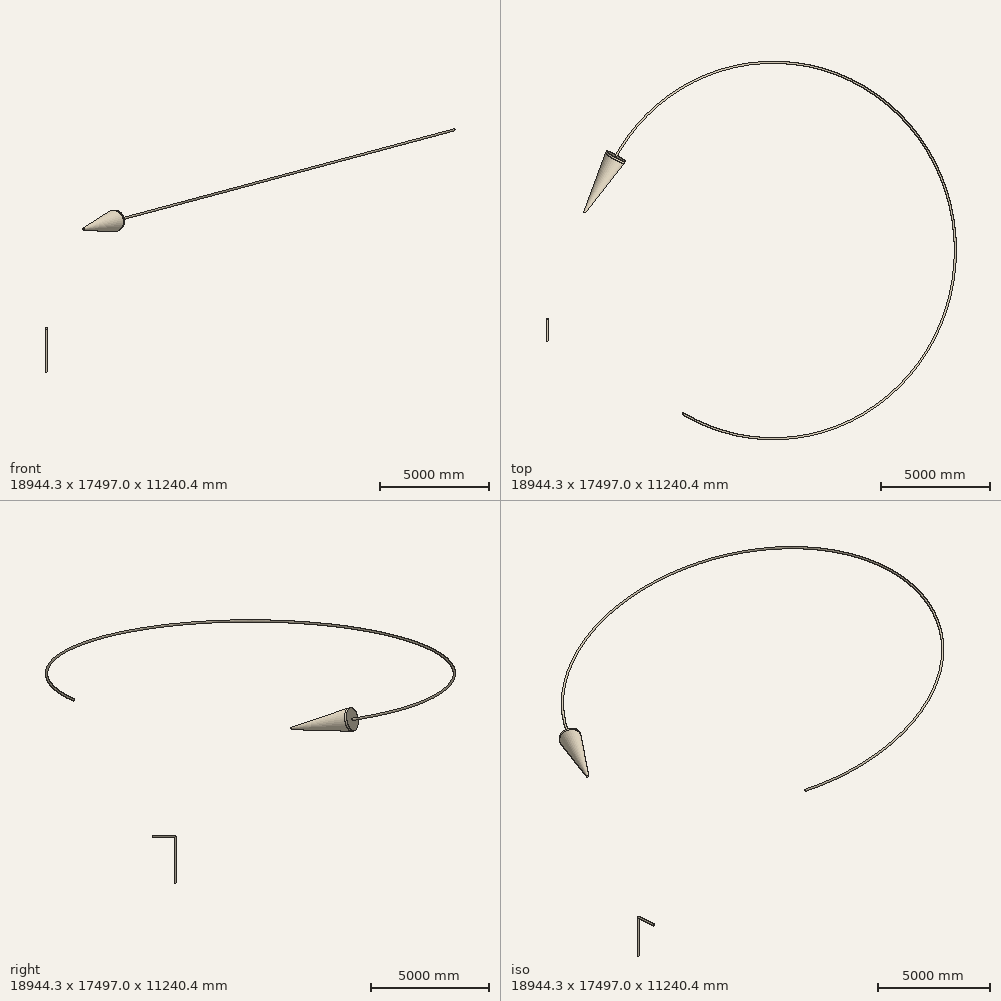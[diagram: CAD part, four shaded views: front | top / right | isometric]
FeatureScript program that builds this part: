
annotation { "Feature Type Name" : "Feature", "Feature Type Description" : "" }
export const myFeature = defineFeature(function(context is Context, id is Id, definition is map)
    precondition{}
    {
        {
            var Q0;
            Q0=qCreatedBy(makeId("Top.planeOp"),FACE);
            var sketch = newSketch(context, id + "F0", { "sketchPlane" : qUnion([Q0])});
            skArc(sketch, "E0", {"start": v(8698.48, 0) * mm, "mid": v(14849.24, 14849.24) * mm, "end": v(0, 8698.48) * mm});
            skSolve(sketch);
        }
        {
            var Q0;
            Q0=sQuery(id+"F0.wireOp",EDGE,"E0");
            var Q1;
            Q1=sQuery(id+"F0.wireOp",VERTEX,"E0.start");
            cPlane(context, id + "F1", {"entities" : qUnion([Q0, Q1]), "cplaneType" : CPlaneType.CURVE_POINT, "offset" : 25 * mm, "width" : 150 * mm, "height" : 150 * mm});
        }
        {
            var Q0;
            Q0=qCreatedBy(id+"F1.planeOp",FACE);
            var sketch = newSketch(context, id + "F2", { "sketchPlane" : qUnion([Q0])});
            skCircle(sketch, "E1", {"center": v(0, 0) * mm, "radius": 50 * mm});
            skSolve(sketch);
        }
        {
            var Q0;
            Q0 = qSketchRegion(id + "F2", true);
            var Q1;
            Q1=sQuery(id+"F0.wireOp",EDGE,"E0");
            sweep(context, id + "F3", {"profiles" : qUnion([Q0]), "path" : qUnion([Q1])});
        }
        {
            var Q0;
            Q0=makeQuery(id+"F3.opSweep","CAP_FACE",FACE,{"disambiguationData":[OSD([sQuery(id+"F0.wireOp",VERTEX,"E0.end"),sQuery(id+"F2.wireOp",EDGE,"E1")])],"isStart":false});
            var sketch = newSketch(context, id + "F4", { "sketchPlane" : qUnion([Q0])});
            skCircle(sketch, "E2", {"center": v(0, 0) * mm, "radius": 500 * mm});
            skSolve(sketch);
        }
        {
            var Q0;
            Q0 = qSketchRegion(id + "F4", true);
            extrude(context, id + "F5", {"entities" : qUnion([Q0]), "operationType" : NewBodyOperationType.ADD, "depth" : 3000 * mm, "offsetDistance" : 25 * mm});
        }
        {
            var Q0;
            Q0=makeQuery(id+"F5.opExtrude","CAP_EDGE",EDGE,{"disambiguationData":[OSD([sQuery(id+"F4.wireOp",EDGE,"E2")])],"isStart":false});
            chamfer(context, id + "F6", {"entities" : qUnion([Q0]), "chamferType" : ChamferType.TWO_OFFSETS, "width1" : 2900 * mm, "oppositeDirection" : true, "width2" : 450 * mm, "tangentPropagation" : true});
        }
        {
            var Q0;
            Q0=qCreatedBy(makeId("Top.planeOp"),FACE);
            var sketch = newSketch(context, id + "F7", { "sketchPlane" : qUnion([Q0])});
            skCircle(sketch, "E3", {"center": v(0, 0) * mm, "radius": 50 * mm});
            skSolve(sketch);
        }
        {
            var Q0;
            Q0 = qSketchRegion(id + "F7", true);
            extrude(context, id + "F8", {"entities" : qUnion([Q0]), "oppositeDirection" : true, "depth" : 2000 * mm, "offsetDistance" : 25 * mm});
        }
        {
            var Q0;
            Q0=makeQuery(id+"F3.opSweep","SWEPT_BODY",BODY,{"disambiguationData":[OSD([sQuery(id+"F0.wireOp",EDGE,"E0"),sQuery(id+"F2.wireOp",EDGE,"E1")])]});
            var Q1;
            Q1=makeQuery(id+"F8.opExtrude","SWEPT_FACE",FACE,{"disambiguationData":[OSD([sQuery(id+"F7.wireOp",EDGE,"E3")])]});
            transform(context, id + "F9", {"entities" : qUnion([Q0]), "transformType" : TransformType.ROTATION, "transformAxis" : qUnion([Q1]), "angle" : 30 * degree, "oppositeDirection" : true, "makeCopy" : false});
        }
        {
            var Q0;
            Q0=makeQuery(id+"F3.opSweep","SWEPT_BODY",BODY,{"disambiguationData":[OSD([sQuery(id+"F0.wireOp",EDGE,"E0"),sQuery(id+"F2.wireOp",EDGE,"E1")])]});
            transform(context, id + "F10", {"entities" : qUnion([Q0]), "transformType" : TransformType.TRANSLATION_3D, "dx" : 0 * mm, "dy" : 0 * mm, "dz" : 4000 * mm, "makeCopy" : false});
        }
        {
            var Q0;
            Q0=qCreatedBy(makeId("Front.planeOp"),FACE);
            var sketch = newSketch(context, id + "F11", { "sketchPlane" : qUnion([Q0])});
            skCircle(sketch, "E4", {"center": v(0, 0) * mm, "radius": 50 * mm});
            skSolve(sketch);
        }
        {
            var Q0;
            Q0 = qSketchRegion(id + "F11", true);
            extrude(context, id + "F12", {"entities" : qUnion([Q0]), "operationType" : NewBodyOperationType.ADD, "depth" : 1000 * mm, "offsetDistance" : 25 * mm});
        }
        {
            var Q0;
            Q0=makeQuery(id+"F3.opSweep","SWEPT_BODY",BODY,{"disambiguationData":[OSD([sQuery(id+"F0.wireOp",EDGE,"E0"),sQuery(id+"F2.wireOp",EDGE,"E1")])]});
            var Q1;
            Q1=makeQuery(id+"F12.opExtrude","SWEPT_FACE",FACE,{"disambiguationData":[OSD([sQuery(id+"F11.wireOp",EDGE,"E4")])]});
            transform(context, id + "F13", {"entities" : qUnion([Q0]), "transformType" : TransformType.ROTATION, "transformAxis" : qUnion([Q1]), "angle" : 15 * degree, "oppositeDirection" : true, "makeCopy" : false});
        }
    });
